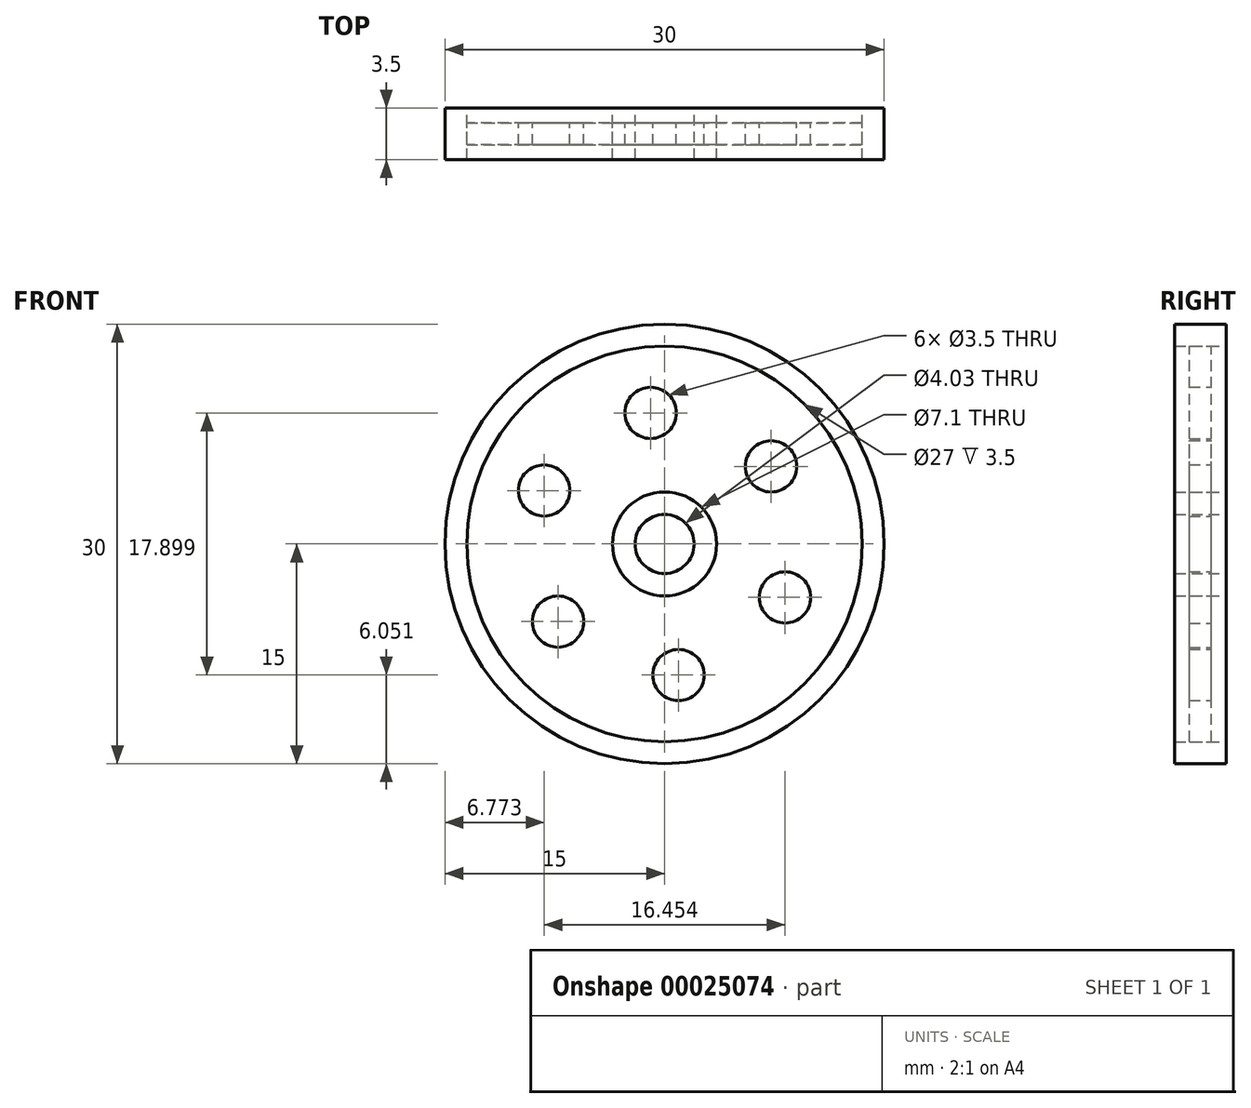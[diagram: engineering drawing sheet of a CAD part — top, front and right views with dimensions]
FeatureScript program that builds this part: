
annotation { "Feature Type Name" : "Feature", "Feature Type Description" : "" }
export const myFeature = defineFeature(function(context is Context, id is Id, definition is map)
    precondition{}
    {
        {
            var Q0;
            Q0=qCreatedBy(makeId("Front.planeOp"),FACE);
            var sketch = newSketch(context, id + "F0", { "sketchPlane" : qUnion([Q0])});
            skCircle(sketch, "E0", {"center": v(0, 0) * mm, "radius": 15 * mm});
            skCircle(sketch, "E1", {"center": v(0, 0) * mm, "radius": 3.55 * mm});
            skCircle(sketch, "E2", {"center": v(0, 0) * mm, "radius": 2.02 * mm});
            skCircle(sketch, "E3", {"center": v(0, 0) * mm, "radius": 13.5 * mm});
            skCircle(sketch, "E4", {"center": v(0, 0) * mm, "radius": 9 * mm});
            skCircle(sketch, "E5", {"center": v(-0.95, 8.95) * mm, "radius": 1.75 * mm});
            skCircle(sketch, "E6.1.0", {"center": v(-8.23, 3.65) * mm, "radius": 1.75 * mm});
            skCircle(sketch, "E6.2.0", {"center": v(-7.27, -5.3) * mm, "radius": 1.75 * mm});
            skCircle(sketch, "E6.3.0", {"center": v(0.95, -8.95) * mm, "radius": 1.75 * mm});
            skCircle(sketch, "E6.4.0", {"center": v(8.23, -3.65) * mm, "radius": 1.75 * mm});
            skCircle(sketch, "E6.5.0", {"center": v(7.27, 5.3) * mm, "radius": 1.75 * mm});
            skSolve(sketch);
        }
        {
            var Q0;
            Q0=makeQuery(id+"F0.imprint","IMPRINT",FACE,{"disambiguationData":[TD([[makeQuery(id+"F0.imprint","IMPRINT",EDGE,{"derivedFrom":sQuery(id+"F0.wireOp",EDGE,"E0")}),1.0]])]});
            extrude(context, id + "F1", {"entities" : qUnion([Q0]), "depth" : 3.5 * mm});
        }
        {
            var Q0;
            Q0=makeQuery(id+"F0.imprint","IMPRINT",FACE,{"disambiguationData":[TD([[makeQuery(id+"F0.imprint","IMPRINT",EDGE,{"derivedFrom":sQuery(id+"F0.wireOp",EDGE,"E1")}),1.0]])]});
            extrude(context, id + "F2", {"entities" : qUnion([Q0]), "depth" : 3.5 * mm});
        }
        {
            var Q0;
            Q0=makeQuery(id+"F0.imprint","IMPRINT",FACE,{"disambiguationData":[TD([[makeQuery(id+"F0.imprint","IMPRINT",EDGE,{"derivedFrom":sQuery(id+"F0.wireOp",EDGE,"E3")}),1.0]])]});
            var Q1;
            Q1=makeQuery(id+"F0.imprint","IMPRINT",FACE,{"disambiguationData":[TD([[makeQuery(id+"F0.imprint","IMPRINT",EDGE,{"derivedFrom":sQuery(id+"F0.wireOp",EDGE,"E1")}),-1.0]])]});
            extrude(context, id + "F3", {"entities" : qUnion([Q0, Q1]), "depth" : 2.5 * mm});
        }
        {
            var Q0;
            Q0=makeQuery(id+"F3.opExtrude","CAP_FACE",FACE,{"disambiguationData":[OSD([sQuery(id+"F0.wireOp",EDGE,"E1"),sQuery(id+"F0.wireOp",EDGE,"E3"),sQuery(id+"F0.wireOp",EDGE,"E5"),sQuery(id+"F0.wireOp",EDGE,"E6.1.0"),sQuery(id+"F0.wireOp",EDGE,"E6.2.0"),sQuery(id+"F0.wireOp",EDGE,"E6.3.0"),sQuery(id+"F0.wireOp",EDGE,"E6.4.0"),sQuery(id+"F0.wireOp",EDGE,"E6.5.0")])],"isStart":true});
            extrude(context, id + "F4", {"entities" : qUnion([Q0]), "operationType" : NewBodyOperationType.REMOVE, "oppositeDirection" : true, "depth" : 1 * mm});
        }
    });
